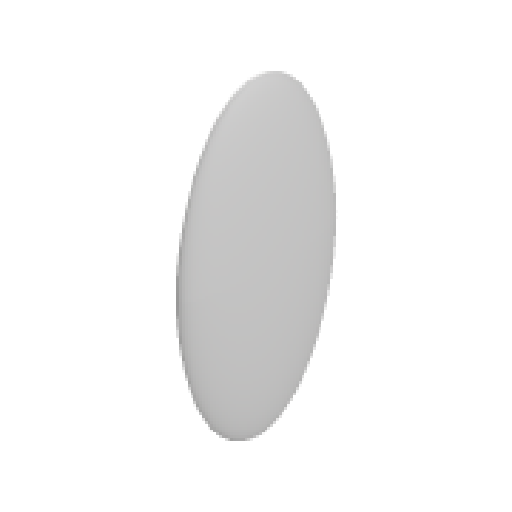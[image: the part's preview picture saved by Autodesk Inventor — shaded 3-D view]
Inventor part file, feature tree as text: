
AUTODESK INVENTOR PART (.ipt)
format: ipt  version: 2023 (Build 270158000, 158)  size: 408,064 bytes
history: native  units: in
note: dims shown in document units (in); Inventor stores cm internally (conversion verified against a paired STEP export)
features: sketch x4, mirror x2, loft x1
ambient origin geometry x8: Origin, YZ Plane, XZ Plane, XY Plane, X Axis, Y Axis, Z Axis, Center Point
bodies: Solid1 (feature_tree)
feature tree (7):
  sketch  "Sketch1"  dims[d0=19.685in d1=4.9213in]
  sketch  "Sketch2"  dims[d2=39.3701in]
  sketch  "Sketch3"  dims[d3=0.0in d4=90.0deg]
  loft  "Loft1"
  mirror  "Mirror1"
  mirror  "Mirror2"
  sketch  "Sketch4"  dims[d5=0.0in d6=90.0deg d7=0.0in d8=90.0deg]
